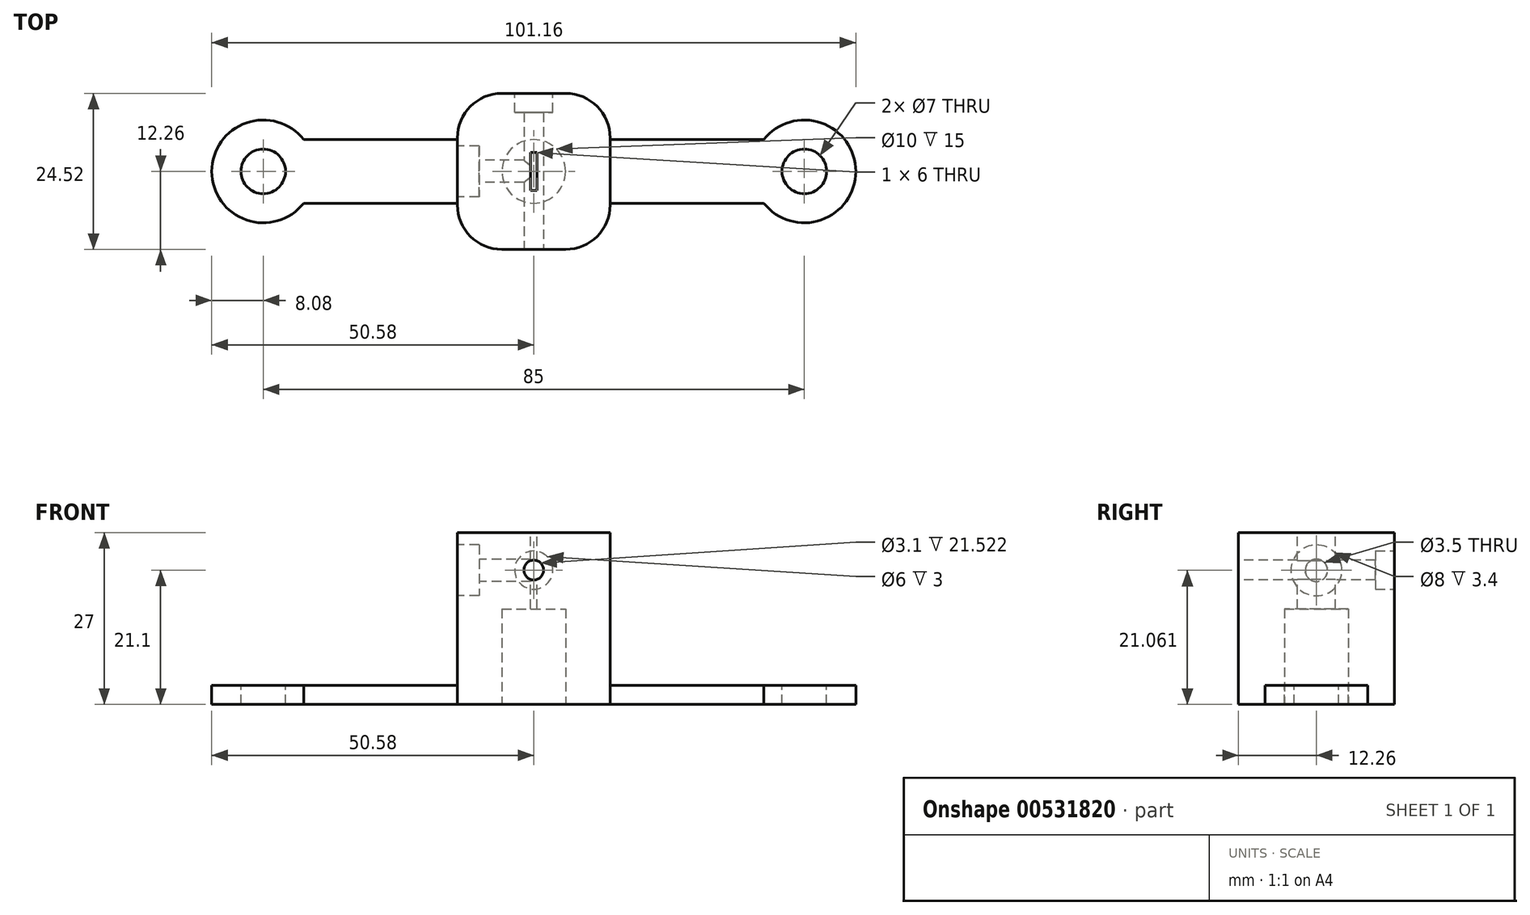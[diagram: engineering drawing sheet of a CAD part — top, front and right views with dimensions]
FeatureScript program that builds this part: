
annotation { "Feature Type Name" : "Feature", "Feature Type Description" : "" }
export const myFeature = defineFeature(function(context is Context, id is Id, definition is map)
    precondition{}
    {
        {
            var Q0;
            Q0=qCreatedBy(makeId("Top.planeOp"),FACE);
            var sketch = newSketch(context, id + "F0", { "sketchPlane" : qUnion([Q0])});
            skLineSegment(sketch, "E0.bottom", {"start": v(42.5, -5) * mm, "end": v(-42.5, -5) * mm});
            skLineSegment(sketch, "E0.top", {"start": v(42.5, 5) * mm, "end": v(-42.5, 5) * mm});
            skLineSegment(sketch, "E0.left", {"start": v(42.5, -5) * mm, "end": v(42.5, 5) * mm});
            skLineSegment(sketch, "E0.right", {"start": v(-42.5, -5) * mm, "end": v(-42.5, 5) * mm});
            skPoint(sketch, "E0.middle", {"position": v(0, 0) * mm});
            skCircle(sketch, "E1", {"center": v(-42.5, 0) * mm, "radius": 8.08 * mm});
            skCircle(sketch, "E2.MirrorC", {"center": v(42.5, 0) * mm, "radius": 8.08 * mm});
            skSolve(sketch);
        }
        {
            var Q0;
            {var subQ0=sQuery(id+"F0.wireOp",EDGE,"E0.left");Q0=makeQuery(id+"F0.imprint","IMPRINT",FACE,{"disambiguationData":[TD([[makeQuery(id+"F0.imprint","IMPRINT",EDGE,{"derivedFrom":subQ0}),-1.0]])]});}
            var Q1;
            {var subQ0=sQuery(id+"F0.wireOp",EDGE,"E0.right");Q1=makeQuery(id+"F0.imprint","IMPRINT",FACE,{"disambiguationData":[TD([[makeQuery(id+"F0.imprint","IMPRINT",EDGE,{"derivedFrom":subQ0}),1.0]])]});}
            var Q2;
            {var subQ0=sQuery(id+"F0.wireOp",EDGE,"E0.left");Q2=makeQuery(id+"F0.imprint","IMPRINT",FACE,{"disambiguationData":[TD([[makeQuery(id+"F0.imprint","IMPRINT",EDGE,{"derivedFrom":subQ0}),1.0]])]});}
            var Q3;
            {var subQ0=sQuery(id+"F0.wireOp",EDGE,"E2.MirrorC");var subQ1=sQuery(id+"F0.wireOp",EDGE,"E0.bottom");var subQ2=makeQuery(id+"F0.imprint","INTERSECT",VERTEX,{"derivedFrom":[subQ1,subQ0]});Q3=makeQuery(id+"F0.imprint","IMPRINT",FACE,{"disambiguationData":[TD([[makeQuery(id+"F0.imprint","IMPRINT",EDGE,{"disambiguationData":[TD([[subQ2,-1.0]])],"derivedFrom":subQ1}),-1.0]])]});}
            var Q4;
            {var subQ0=sQuery(id+"F0.wireOp",EDGE,"E0.right");Q4=makeQuery(id+"F0.imprint","IMPRINT",FACE,{"disambiguationData":[TD([[makeQuery(id+"F0.imprint","IMPRINT",EDGE,{"derivedFrom":subQ0}),-1.0]])]});}
            extrude(context, id + "F1", {"entities" : qUnion([Q0, Q1, Q2, Q3, Q4]), "depth" : 3 * mm, "offsetDistance" : 25 * mm});
        }
        {
            var Q0;
            Q0=makeQuery(id+"F1.opExtrude","CAP_FACE",FACE,{"disambiguationData":[OSD([sQuery(id+"F0.wireOp",EDGE,"E0.bottom"),sQuery(id+"F0.wireOp",EDGE,"E0.top"),sQuery(id+"F0.wireOp",EDGE,"E1"),sQuery(id+"F0.wireOp",EDGE,"E2.MirrorC")])],"isStart":false});
            var sketch = newSketch(context, id + "F2", { "sketchPlane" : qUnion([Q0])});
            skCircle(sketch, "E3", {"center": v(-42.5, 0) * mm, "radius": 3.05 * mm});
            skCircle(sketch, "E4.MirrorC", {"center": v(42.5, 0) * mm, "radius": 3.05 * mm});
            skSolve(sketch);
        }
        {
            var Q0;
            Q0=sQuery(id+"F2.wireOp",VERTEX,"E3.center");
            var Q1;
            Q1=sQuery(id+"F2.wireOp",VERTEX,"E4.MirrorC.center");
            var Q2;
            Q2=makeQuery(id+"F1.opExtrude","SWEPT_BODY",BODY,{"disambiguationData":[OSD([sQuery(id+"F0.wireOp",EDGE,"E0.bottom"),sQuery(id+"F0.wireOp",EDGE,"E0.top"),sQuery(id+"F0.wireOp",EDGE,"E1"),sQuery(id+"F0.wireOp",EDGE,"E2.MirrorC")])]});
            hole(context, id + "F3", {"style" : HoleStyle.SIMPLE, "endStyle" : HoleEndStyle.THROUGH, "holeDiameter" : 7 * mm, "isTappedThrough" : true, "tappedDepth" : 12 * mm, "tapClearance" : 3, "locations" : qUnion([Q0, Q1]), "scope" : qUnion([Q2])});
        }
        {
            var Q0;
            Q0=qCreatedBy(makeId("Top.planeOp"),FACE);
            var sketch = newSketch(context, id + "F4", { "sketchPlane" : qUnion([Q0])});
            skLineSegment(sketch, "E5.bottom", {"start": v(12, 12.26) * mm, "end": v(-12, 12.26) * mm});
            skLineSegment(sketch, "E5.top", {"start": v(12, -12.26) * mm, "end": v(-12, -12.26) * mm});
            skLineSegment(sketch, "E5.left", {"start": v(12, 12.26) * mm, "end": v(12, -12.26) * mm});
            skLineSegment(sketch, "E5.right", {"start": v(-12, 12.26) * mm, "end": v(-12, -12.26) * mm});
            skPoint(sketch, "E5.middle", {"position": v(0, 0) * mm});
            skSolve(sketch);
        }
        {
            var Q0;
            Q0 = qSketchRegion(id + "F4", true);
            extrude(context, id + "F5", {"entities" : qUnion([Q0]), "operationType" : NewBodyOperationType.ADD, "depth" : 27 * mm, "offsetDistance" : 25 * mm});
        }
        {
            var Q0;
            Q0=qCreatedBy(makeId("Front.planeOp"),FACE);
            var sketch = newSketch(context, id + "F6", { "sketchPlane" : qUnion([Q0])});
            skCircle(sketch, "E6", {"center": v(0, 21.1) * mm, "radius": 1.55 * mm});
            skSolve(sketch);
        }
        {
            var Q0;
            Q0 = qSketchRegion(id + "F6", true);
            extrude(context, id + "F7", {"entities" : qUnion([Q0]), "operationType" : NewBodyOperationType.REMOVE, "endBound" : BoundingType.SYMMETRIC, "oppositeDirection" : true, "depth" : 25 * mm, "offsetDistance" : 25 * mm});
        }
        {
            var Q0;
            Q0=makeQuery(id+"F5.opExtrude","SWEPT_FACE",FACE,{"disambiguationData":[OSD([sQuery(id+"F4.wireOp",EDGE,"E5.right")])]});
            var sketch = newSketch(context, id + "F8", { "sketchPlane" : qUnion([Q0])});
            skCircle(sketch, "E7", {"center": v(0, 21.06) * mm, "radius": 1.75 * mm});
            skSolve(sketch);
        }
        {
            var Q0;
            Q0 = qSketchRegion(id + "F8", true);
            extrude(context, id + "F9", {"entities" : qUnion([Q0]), "operationType" : NewBodyOperationType.REMOVE, "oppositeDirection" : true, "depth" : 12 * mm, "offsetDistance" : 25 * mm});
        }
        {
            var Q0;
            Q0=makeQuery(id+"F5.opExtrude","SWEPT_FACE",FACE,{"disambiguationData":[OSD([sQuery(id+"F4.wireOp",EDGE,"E5.right")])]});
            var sketch = newSketch(context, id + "F10", { "sketchPlane" : qUnion([Q0])});
            skCircle(sketch, "E8", {"center": v(0, 21.06) * mm, "radius": 4 * mm});
            skSolve(sketch);
        }
        {
            var Q0;
            Q0 = qSketchRegion(id + "F10", true);
            extrude(context, id + "F11", {"entities" : qUnion([Q0]), "operationType" : NewBodyOperationType.REMOVE, "oppositeDirection" : true, "depth" : 3.4 * mm, "offsetDistance" : 25 * mm});
        }
        {
            var Q0;
            Q0=makeQuery(id+"F5.opExtrude","SWEPT_EDGE",EDGE,{"disambiguationData":[OSD([sQuery(id+"F4.wireOp",EDGE,"E5.bottom"),sQuery(id+"F4.wireOp",EDGE,"E5.right")])]});
            fillet(context, id + "F12", {"entities" : qUnion([Q0]), "radius" : 7 * mm, "tangentPropagation" : true, "allowEdgeOverflow" : false});
        }
        {
            var Q0;
            Q0=makeQuery(id+"F5.opExtrude","SWEPT_EDGE",EDGE,{"disambiguationData":[OSD([sQuery(id+"F4.wireOp",EDGE,"E5.bottom"),sQuery(id+"F4.wireOp",EDGE,"E5.left")])]});
            fillet(context, id + "F13", {"entities" : qUnion([Q0]), "radius" : 7 * mm, "tangentPropagation" : true, "allowEdgeOverflow" : false});
        }
        {
            var Q0;
            Q0=makeQuery(id+"F5.opExtrude","SWEPT_EDGE",EDGE,{"disambiguationData":[OSD([sQuery(id+"F4.wireOp",EDGE,"E5.top"),sQuery(id+"F4.wireOp",EDGE,"E5.right")])]});
            fillet(context, id + "F14", {"entities" : qUnion([Q0]), "radius" : 7 * mm, "tangentPropagation" : true, "allowEdgeOverflow" : false});
        }
        {
            var Q0;
            Q0=makeQuery(id+"F5.opExtrude","SWEPT_EDGE",EDGE,{"disambiguationData":[OSD([sQuery(id+"F4.wireOp",EDGE,"E5.top"),sQuery(id+"F4.wireOp",EDGE,"E5.left")])]});
            fillet(context, id + "F15", {"entities" : qUnion([Q0]), "radius" : 7 * mm, "tangentPropagation" : true, "allowEdgeOverflow" : false});
        }
        {
            var Q0;
            Q0=makeQuery(id+"F5.opExtrude","CAP_FACE",FACE,{"disambiguationData":[OSD([sQuery(id+"F4.wireOp",EDGE,"E5.bottom"),sQuery(id+"F4.wireOp",EDGE,"E5.top"),sQuery(id+"F4.wireOp",EDGE,"E5.left"),sQuery(id+"F4.wireOp",EDGE,"E5.right")])],"isStart":false});
            var sketch = newSketch(context, id + "F16", { "sketchPlane" : qUnion([Q0])});
            skLineSegment(sketch, "E9.bottom", {"start": v(-0.5, 3) * mm, "end": v(0.5, 3) * mm});
            skLineSegment(sketch, "E9.top", {"start": v(-0.5, -3) * mm, "end": v(0.5, -3) * mm});
            skLineSegment(sketch, "E9.left", {"start": v(-0.5, 3) * mm, "end": v(-0.5, -3) * mm});
            skLineSegment(sketch, "E9.right", {"start": v(0.5, 3) * mm, "end": v(0.5, -3) * mm});
            skPoint(sketch, "E9.middle", {"position": v(0, 0) * mm});
            skSolve(sketch);
        }
        {
            var Q0;
            Q0 = qSketchRegion(id + "F16", true);
            extrude(context, id + "F17", {"entities" : qUnion([Q0]), "operationType" : NewBodyOperationType.REMOVE, "oppositeDirection" : true, "depth" : 14 * mm, "offsetDistance" : 25 * mm});
        }
        {
            var Q0;
            Q0=makeQuery(id+"F5.boolean.opBoolean","MERGE",FACE,{"derivedFrom":[makeQuery(id+"F1.opExtrude","CAP_FACE",FACE,{"disambiguationData":[OSD([sQuery(id+"F0.wireOp",EDGE,"E0.bottom"),sQuery(id+"F0.wireOp",EDGE,"E0.top"),sQuery(id+"F0.wireOp",EDGE,"E1"),sQuery(id+"F0.wireOp",EDGE,"E2.MirrorC")])],"isStart":true}),makeQuery(id+"F5.opExtrude","CAP_FACE",FACE,{"disambiguationData":[OSD([sQuery(id+"F4.wireOp",EDGE,"E5.bottom"),sQuery(id+"F4.wireOp",EDGE,"E5.top"),sQuery(id+"F4.wireOp",EDGE,"E5.left"),sQuery(id+"F4.wireOp",EDGE,"E5.right")])],"isStart":true})]});
            var sketch = newSketch(context, id + "F18", { "sketchPlane" : qUnion([Q0])});
            skCircle(sketch, "E10", {"center": v(0, 0) * mm, "radius": 5 * mm});
            skSolve(sketch);
        }
        {
            var Q0;
            Q0 = qSketchRegion(id + "F18", true);
            extrude(context, id + "F19", {"entities" : qUnion([Q0]), "operationType" : NewBodyOperationType.REMOVE, "oppositeDirection" : true, "depth" : 15 * mm, "offsetDistance" : 25 * mm});
        }
        {
            var Q0;
            Q0=makeQuery(id+"F5.opExtrude","SWEPT_FACE",FACE,{"disambiguationData":[OSD([sQuery(id+"F4.wireOp",EDGE,"E5.bottom")])]});
            var sketch = newSketch(context, id + "F20", { "sketchPlane" : qUnion([Q0])});
            skCircle(sketch, "E11", {"center": v(0, 21.1) * mm, "radius": 3 * mm});
            skSolve(sketch);
        }
        {
            var Q0;
            Q0=makeQuery(id+"F20.imprint","IMPRINT",FACE,{"disambiguationData":[TD([[makeQuery(id+"F20.imprint","IMPRINT",EDGE,{"derivedFrom":sQuery(id+"F20.wireOp",EDGE,"E11")}),1.0]])]});
            var Q1;
            Q1=sQuery(id+"F20.wireOp",EDGE,"E11");
            extrude(context, id + "F21", {"entities" : qUnion([Q0]), "operationType" : NewBodyOperationType.REMOVE, "surfaceEntities" : qUnion([Q1]), "oppositeDirection" : true, "depth" : 3 * mm, "offsetDistance" : 25 * mm});
        }
    });
